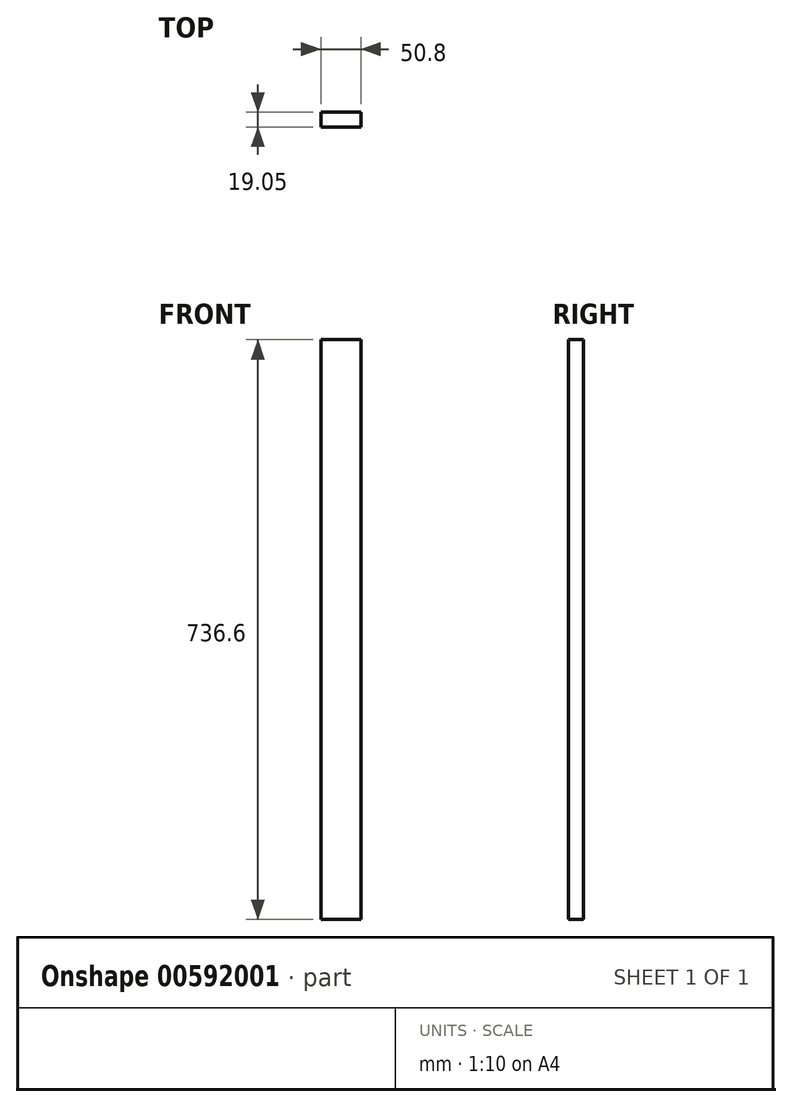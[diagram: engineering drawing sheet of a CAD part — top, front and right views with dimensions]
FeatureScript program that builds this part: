
annotation { "Feature Type Name" : "Feature", "Feature Type Description" : "" }
export const myFeature = defineFeature(function(context is Context, id is Id, definition is map)
    precondition{}
    {
        {
            var Q0;
            Q0=qCreatedBy(makeId("Front.planeOp"),FACE);
            var sketch = newSketch(context, id + "F0", { "sketchPlane" : qUnion([Q0])});
            skLineSegment(sketch, "E0.bottom", {"start": v(-32.64, 725.79) * mm, "end": v(18.16, 725.79) * mm});
            skLineSegment(sketch, "E0.top", {"start": v(-32.64, -10.81) * mm, "end": v(18.16, -10.81) * mm});
            skLineSegment(sketch, "E0.left", {"start": v(-32.64, 725.79) * mm, "end": v(-32.64, -10.81) * mm});
            skLineSegment(sketch, "E0.right", {"start": v(18.16, 725.79) * mm, "end": v(18.16, -10.81) * mm});
            skSolve(sketch);
        }
        {
            var Q0;
            Q0 = qSketchRegion(id + "F0", true);
            extrude(context, id + "F1", {"entities" : qUnion([Q0]), "depth" : 19.05 * mm, "offsetDistance" : 25.4 * mm});
        }
    });
